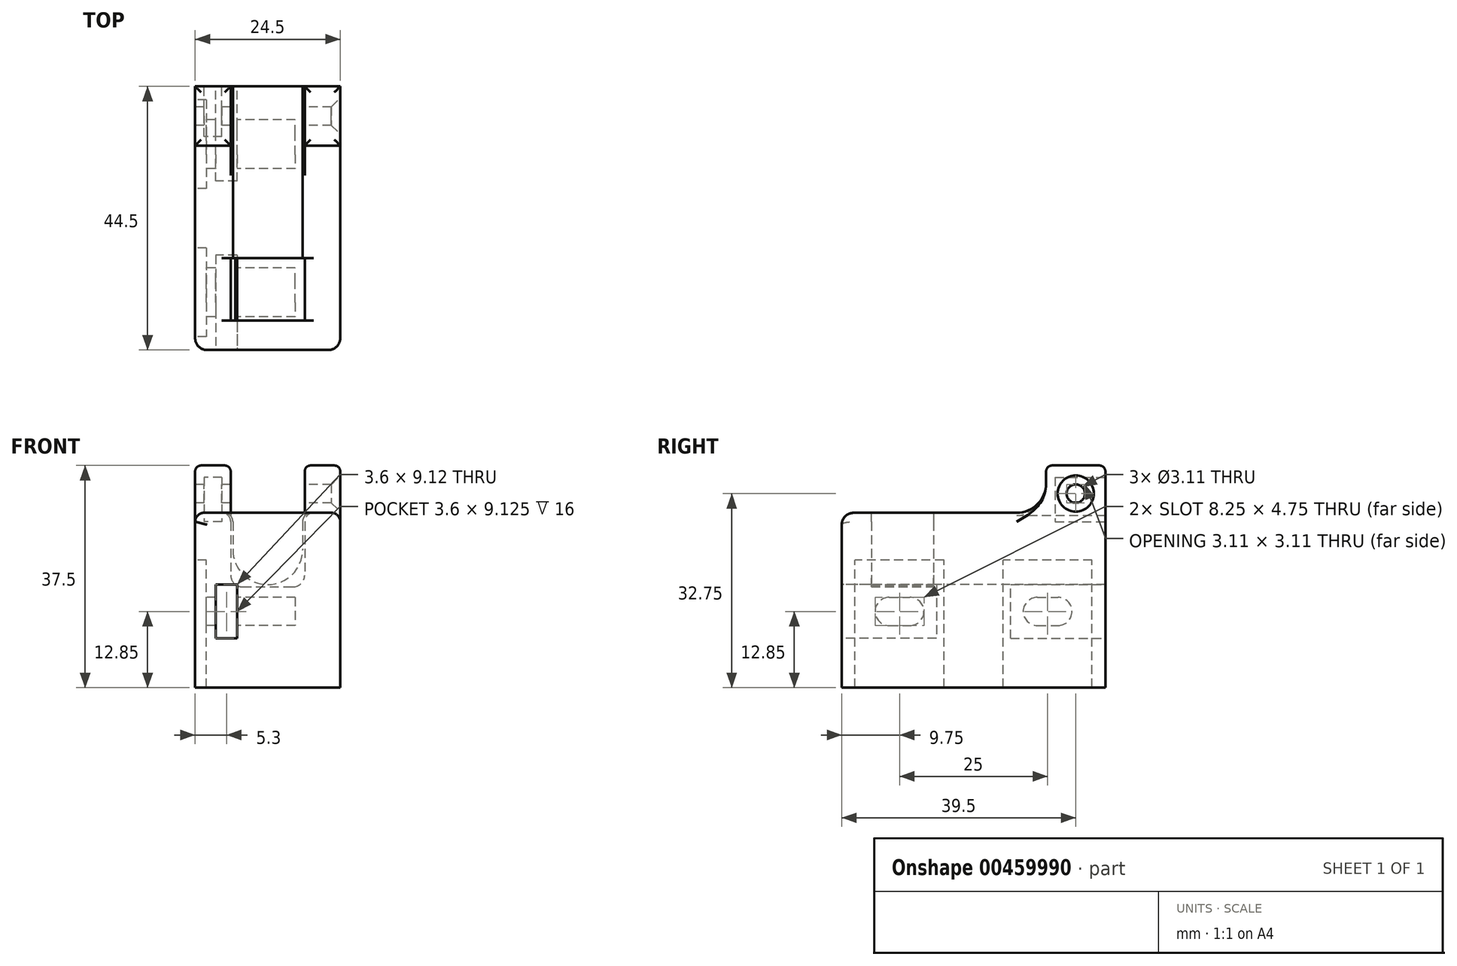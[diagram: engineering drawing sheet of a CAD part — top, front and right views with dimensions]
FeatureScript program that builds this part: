
annotation { "Feature Type Name" : "Feature", "Feature Type Description" : "" }
export const myFeature = defineFeature(function(context is Context, id is Id, definition is map)
    precondition{}
    {
        {
            var Q0;
            Q0=qCreatedBy(makeId("Front.planeOp"),FACE);
            var sketch = newSketch(context, id + "F0", { "sketchPlane" : qUnion([Q0])});
            skLineSegment(sketch, "E0.bottom", {"start": v(-6.25, 6.25) * mm, "end": v(6.25, 6.25) * mm, "construction": true});
            skLineSegment(sketch, "E0.top", {"start": v(-4.25, -6.25) * mm, "end": v(4.25, -6.25) * mm});
            skLineSegment(sketch, "E0.left", {"start": v(-6.25, 4.75) * mm, "end": v(-6.25, -4.25) * mm});
            skLineSegment(sketch, "E0.right", {"start": v(6.25, 4.75) * mm, "end": v(6.25, -4.25) * mm});
            skPoint(sketch, "E0.middle", {"position": v(0, 0) * mm});
            skLineSegment(sketch, "E1.bottom", {"start": v(-10.75, -11.25) * mm, "end": v(10.75, -11.25) * mm});
            skLineSegment(sketch, "E1.left", {"start": v(-12.25, -9.75) * mm, "end": v(-12.25, 4.75) * mm});
            skLineSegment(sketch, "E1.right", {"start": v(12.25, -9.75) * mm, "end": v(12.25, 4.75) * mm});
            skLineSegment(sketch, "E2", {"start": v(-7.75, 6.25) * mm, "end": v(-10.75, 6.25) * mm});
            skLineSegment(sketch, "E3", {"start": v(7.75, 6.25) * mm, "end": v(10.75, 6.25) * mm});
            skPoint(sketch, "E4.visualSharp", {"position": v(-6.25, -6.25) * mm});
            skArc(sketch, "E4.filletArc", {"start": v(-6.25, -4.25) * mm, "mid": v(-5.66, -5.66) * mm, "end": v(-4.25, -6.25) * mm});
            skPoint(sketch, "E5.visualSharp", {"position": v(6.25, -6.25) * mm});
            skArc(sketch, "E5.filletArc", {"start": v(4.25, -6.25) * mm, "mid": v(5.66, -5.66) * mm, "end": v(6.25, -4.25) * mm});
            skPoint(sketch, "E6.visualSharp", {"position": v(-6.25, 6.25) * mm});
            skArc(sketch, "E6.filletArc", {"start": v(-6.25, 4.75) * mm, "mid": v(-6.69, 5.81) * mm, "end": v(-7.75, 6.25) * mm});
            skPoint(sketch, "E7.visualSharp", {"position": v(6.25, 6.25) * mm});
            skArc(sketch, "E7.filletArc", {"start": v(7.75, 6.25) * mm, "mid": v(6.69, 5.81) * mm, "end": v(6.25, 4.75) * mm});
            skLineSegment(sketch, "E8", {"start": v(6.25, 0.25) * mm, "end": v(12.25, 0.25) * mm, "construction": true});
            skLineSegment(sketch, "E9", {"start": v(-6.25, 0.25) * mm, "end": v(-12.25, 0.25) * mm, "construction": true});
            skLineSegment(sketch, "E10", {"start": v(0, -6.25) * mm, "end": v(0, -11.25) * mm, "construction": true});
            skPoint(sketch, "E11.visualSharp", {"position": v(-12.25, 6.25) * mm});
            skArc(sketch, "E11.filletArc", {"start": v(-10.75, 6.25) * mm, "mid": v(-11.81, 5.81) * mm, "end": v(-12.25, 4.75) * mm});
            skPoint(sketch, "E12.visualSharp", {"position": v(-12.25, -11.25) * mm});
            skArc(sketch, "E12.filletArc", {"start": v(-12.25, -9.75) * mm, "mid": v(-11.81, -10.81) * mm, "end": v(-10.75, -11.25) * mm});
            skPoint(sketch, "E13.visualSharp", {"position": v(12.25, -11.25) * mm});
            skArc(sketch, "E13.filletArc", {"start": v(10.75, -11.25) * mm, "mid": v(11.81, -10.81) * mm, "end": v(12.25, -9.75) * mm});
            skPoint(sketch, "E14.visualSharp", {"position": v(12.25, 6.25) * mm});
            skArc(sketch, "E14.filletArc", {"start": v(12.25, 4.75) * mm, "mid": v(11.81, 5.81) * mm, "end": v(10.75, 6.25) * mm});
            skSolve(sketch);
        }
        {
            var Q0;
            Q0=makeQuery(id+"F0.imprint","IMPRINT",FACE,{"disambiguationData":[TD([[makeQuery(id+"F0.imprint","IMPRINT",EDGE,{"derivedFrom":sQuery(id+"F0.wireOp",EDGE,"E0.top")}),-1.0]])]});
            extrude(context, id + "F1", {"entities" : qUnion([Q0]), "depth" : 10.5 * mm});
        }
        {
            var Q0;
            Q0=makeQuery(id+"F1.opExtrude","CAP_FACE",FACE,{"disambiguationData":[OSD([sQuery(id+"F0.wireOp",EDGE,"E0.top"),sQuery(id+"F0.wireOp",EDGE,"E0.left"),sQuery(id+"F0.wireOp",EDGE,"E0.right"),sQuery(id+"F0.wireOp",EDGE,"E1.bottom"),sQuery(id+"F0.wireOp",EDGE,"E1.left"),sQuery(id+"F0.wireOp",EDGE,"E1.right"),sQuery(id+"F0.wireOp",EDGE,"E2"),sQuery(id+"F0.wireOp",EDGE,"E3"),sQuery(id+"F0.wireOp",EDGE,"E4.filletArc"),sQuery(id+"F0.wireOp",EDGE,"E5.filletArc"),sQuery(id+"F0.wireOp",EDGE,"E6.filletArc"),sQuery(id+"F0.wireOp",EDGE,"E7.filletArc"),sQuery(id+"F0.wireOp",EDGE,"E11.filletArc"),sQuery(id+"F0.wireOp",EDGE,"E12.filletArc"),sQuery(id+"F0.wireOp",EDGE,"E13.filletArc"),sQuery(id+"F0.wireOp",EDGE,"E14.filletArc")])],"isStart":false});
            var sketch = newSketch(context, id + "F2", { "sketchPlane" : qUnion([Q0])});
            skLineSegment(sketch, "E15.bottom", {"start": v(-10.75, -11.25) * mm, "end": v(10.75, -11.25) * mm});
            skLineSegment(sketch, "E15.top", {"start": v(-10.75, 6.25) * mm, "end": v(10.75, 6.25) * mm});
            skLineSegment(sketch, "E15.left", {"start": v(-12.25, -9.75) * mm, "end": v(-12.25, 4.75) * mm});
            skLineSegment(sketch, "E15.right", {"start": v(12.25, -9.75) * mm, "end": v(12.25, 4.75) * mm});
            skPoint(sketch, "E16.visualSharp", {"position": v(-12.25, 6.25) * mm});
            skArc(sketch, "E16.filletArc", {"start": v(-10.75, 6.25) * mm, "mid": v(-11.81, 5.81) * mm, "end": v(-12.25, 4.75) * mm});
            skPoint(sketch, "E17.visualSharp", {"position": v(-12.25, -11.25) * mm});
            skArc(sketch, "E17.filletArc", {"start": v(-12.25, -9.75) * mm, "mid": v(-11.81, -10.81) * mm, "end": v(-10.75, -11.25) * mm});
            skPoint(sketch, "E18.visualSharp", {"position": v(12.25, -11.25) * mm});
            skArc(sketch, "E18.filletArc", {"start": v(10.75, -11.25) * mm, "mid": v(11.81, -10.81) * mm, "end": v(12.25, -9.75) * mm});
            skPoint(sketch, "E19.visualSharp", {"position": v(12.25, 6.25) * mm});
            skArc(sketch, "E19.filletArc", {"start": v(12.25, 4.75) * mm, "mid": v(11.81, 5.81) * mm, "end": v(10.75, 6.25) * mm});
            skSolve(sketch);
        }
        {
            var Q0;
            Q0 = qSketchRegion(id + "F2", true);
            extrude(context, id + "F3", {"entities" : qUnion([Q0]), "operationType" : NewBodyOperationType.ADD, "depth" : 5 * mm, "offsetDistance" : 25 * mm});
        }
        {
            var Q0;
            Q0=makeQuery(id+"F3.opExtrude","SWEPT_FACE",FACE,{"disambiguationData":[OSD([sQuery(id+"F2.wireOp",EDGE,"E15.top")])]});
            var sketch = newSketch(context, id + "F4", { "sketchPlane" : qUnion([Q0])});
            skLineSegment(sketch, "E20", {"start": v(-87.92, 24.65) * mm, "end": v(-21.67, -10.5) * mm});
            skLineSegment(sketch, "E21", {"start": v(-21.67, -10.5) * mm, "end": v(-33.58, -32.94) * mm});
            skLineSegment(sketch, "E22", {"start": v(-33.58, -32.94) * mm, "end": v(-99.83, 2.22) * mm});
            skLineSegment(sketch, "E23", {"start": v(-99.83, 2.22) * mm, "end": v(-87.92, 24.65) * mm});
            skLineSegment(sketch, "E24", {"start": v(-21.67, -10.5) * mm, "end": v(-87.92, -10.5) * mm, "construction": true});
            skLineSegment(sketch, "E25", {"start": v(-87.92, 24.65) * mm, "end": v(-87.92, -10.5) * mm, "construction": true});
            skLineSegment(sketch, "E26", {"start": v(-12.25, -10.5) * mm, "end": v(-12.25, -15.5) * mm, "construction": true});
            skLineSegment(sketch, "E27", {"start": v(12.25, -10.5) * mm, "end": v(12.25, -28.5) * mm, "construction": true});
            skSolve(sketch);
        }
        {
            var Q0;
            Q0 = qSketchRegion(id + "F4", true);
            extrude(context, id + "F5", {"entities" : qUnion([Q0]), "operationType" : NewBodyOperationType.REMOVE, "oppositeDirection" : true, "depth" : 25 * mm});
        }
        {
            var Q0;
            Q0=makeQuery(id+"F1.opExtrude","CAP_FACE",FACE,{"disambiguationData":[OSD([sQuery(id+"F0.wireOp",EDGE,"E0.top"),sQuery(id+"F0.wireOp",EDGE,"E0.left"),sQuery(id+"F0.wireOp",EDGE,"E0.right"),sQuery(id+"F0.wireOp",EDGE,"E1.bottom"),sQuery(id+"F0.wireOp",EDGE,"E1.left"),sQuery(id+"F0.wireOp",EDGE,"E1.right"),sQuery(id+"F0.wireOp",EDGE,"E2"),sQuery(id+"F0.wireOp",EDGE,"E3"),sQuery(id+"F0.wireOp",EDGE,"E4.filletArc"),sQuery(id+"F0.wireOp",EDGE,"E5.filletArc"),sQuery(id+"F0.wireOp",EDGE,"E6.filletArc"),sQuery(id+"F0.wireOp",EDGE,"E7.filletArc"),sQuery(id+"F0.wireOp",EDGE,"E11.filletArc"),sQuery(id+"F0.wireOp",EDGE,"E12.filletArc"),sQuery(id+"F0.wireOp",EDGE,"E13.filletArc"),sQuery(id+"F0.wireOp",EDGE,"E14.filletArc")])],"isStart":true});
            var sketch = newSketch(context, id + "F6", { "sketchPlane" : qUnion([Q0])});
            skArc(sketch, "E28", {"start": v(-5.88, 0) * mm, "mid": v(0, -5.88) * mm, "end": v(5.88, 0) * mm});
            skPoint(sketch, "E29", {"position": v(6.69, 5.81) * mm});
            skLineSegment(sketch, "E30.top", {"start": v(-10.75, -11.25) * mm, "end": v(10.75, -11.25) * mm});
            skLineSegment(sketch, "E30.left", {"start": v(-12.25, 4.75) * mm, "end": v(-12.25, -9.75) * mm});
            skLineSegment(sketch, "E30.right", {"start": v(12.25, 4.75) * mm, "end": v(12.25, -9.75) * mm});
            skLineSegment(sketch, "E31", {"start": v(-10.75, 6.25) * mm, "end": v(-7.38, 6.25) * mm});
            skLineSegment(sketch, "E32", {"start": v(-5.87, 4.75) * mm, "end": v(-5.87, 0) * mm});
            skLineSegment(sketch, "E33", {"start": v(10.75, 6.25) * mm, "end": v(7.38, 6.25) * mm});
            skLineSegment(sketch, "E34", {"start": v(5.87, 4.75) * mm, "end": v(5.88, 0) * mm});
            skPoint(sketch, "E35.visualSharp", {"position": v(-12.25, 6.25) * mm});
            skArc(sketch, "E35.filletArc", {"start": v(-10.75, 6.25) * mm, "mid": v(-11.81, 5.81) * mm, "end": v(-12.25, 4.75) * mm});
            skPoint(sketch, "E36.visualSharp", {"position": v(-5.88, 6.25) * mm});
            skArc(sketch, "E36.filletArc", {"start": v(-5.88, 4.75) * mm, "mid": v(-6.31, 5.81) * mm, "end": v(-7.38, 6.25) * mm});
            skPoint(sketch, "E37.visualSharp", {"position": v(5.88, 6.25) * mm});
            skArc(sketch, "E37.filletArc", {"start": v(7.38, 6.25) * mm, "mid": v(6.31, 5.81) * mm, "end": v(5.88, 4.75) * mm});
            skPoint(sketch, "E38.visualSharp", {"position": v(12.25, 6.25) * mm});
            skArc(sketch, "E38.filletArc", {"start": v(12.25, 4.75) * mm, "mid": v(11.81, 5.81) * mm, "end": v(10.75, 6.25) * mm});
            skPoint(sketch, "E39.visualSharp", {"position": v(12.25, -11.25) * mm});
            skArc(sketch, "E39.filletArc", {"start": v(10.75, -11.25) * mm, "mid": v(11.81, -10.81) * mm, "end": v(12.25, -9.75) * mm});
            skPoint(sketch, "E40.visualSharp", {"position": v(-12.25, -11.25) * mm});
            skArc(sketch, "E40.filletArc", {"start": v(-12.25, -9.75) * mm, "mid": v(-11.81, -10.81) * mm, "end": v(-10.75, -11.25) * mm});
            skSolve(sketch);
        }
        {
            var Q0;
            Q0 = qSketchRegion(id + "F6", true);
            extrude(context, id + "F7", {"entities" : qUnion([Q0]), "operationType" : NewBodyOperationType.ADD, "depth" : 29 * mm, "offsetDistance" : 25 * mm});
        }
        {
            var Q0;
            Q0=makeQuery(id+"F3.opExtrude","CAP_FACE",FACE,{"disambiguationData":[OSD([sQuery(id+"F2.wireOp",EDGE,"E15.bottom"),sQuery(id+"F2.wireOp",EDGE,"E15.top"),sQuery(id+"F2.wireOp",EDGE,"E15.left"),sQuery(id+"F2.wireOp",EDGE,"E15.right"),sQuery(id+"F2.wireOp",EDGE,"E16.filletArc"),sQuery(id+"F2.wireOp",EDGE,"E17.filletArc"),sQuery(id+"F2.wireOp",EDGE,"E18.filletArc"),sQuery(id+"F2.wireOp",EDGE,"E19.filletArc")])],"isStart":false});
            fillet(context, id + "F8", {"entities" : qUnion([Q0]), "radius" : 2 * mm, "tangentPropagation" : true, "allowEdgeOverflow" : false});
        }
        {
            var Q0;
            Q0=makeQuery(id+"F7.boolean.opBoolean","MERGE",FACE,{"derivedFrom":[makeQuery(id+"F3.boolean.opBoolean","MERGE",FACE,{"derivedFrom":[makeQuery(id+"F1.opExtrude","SWEPT_FACE",FACE,{"disambiguationData":[OSD([sQuery(id+"F0.wireOp",EDGE,"E2")])]}),makeQuery(id+"F1.opExtrude","SWEPT_FACE",FACE,{"disambiguationData":[OSD([sQuery(id+"F0.wireOp",EDGE,"E3")])]}),makeQuery(id+"F3.opExtrude","SWEPT_FACE",FACE,{"disambiguationData":[OSD([sQuery(id+"F2.wireOp",EDGE,"E15.top")])]})]}),makeQuery(id+"F7.opExtrude","SWEPT_FACE",FACE,{"disambiguationData":[OSD([sQuery(id+"F6.wireOp",EDGE,"E31")])]}),makeQuery(id+"F7.opExtrude","SWEPT_FACE",FACE,{"disambiguationData":[OSD([sQuery(id+"F6.wireOp",EDGE,"E33")])]})]});
            var sketch = newSketch(context, id + "F9", { "sketchPlane" : qUnion([Q0])});
            skLineSegment(sketch, "E41.bottom", {"start": v(-12.25, 29) * mm, "end": v(-6.25, 29) * mm});
            skLineSegment(sketch, "E41.top", {"start": v(-12.25, 19) * mm, "end": v(-6.25, 19) * mm});
            skLineSegment(sketch, "E41.left", {"start": v(-12.25, 29) * mm, "end": v(-12.25, 19) * mm});
            skLineSegment(sketch, "E41.right", {"start": v(-6.25, 29) * mm, "end": v(-6.25, 19) * mm});
            skLineSegment(sketch, "E42.bottom", {"start": v(6.25, 29) * mm, "end": v(12.25, 29) * mm});
            skLineSegment(sketch, "E42.top", {"start": v(6.25, 19) * mm, "end": v(12.25, 19) * mm});
            skLineSegment(sketch, "E42.left", {"start": v(6.25, 29) * mm, "end": v(6.25, 19) * mm});
            skLineSegment(sketch, "E42.right", {"start": v(12.25, 29) * mm, "end": v(12.25, 19) * mm});
            skSolve(sketch);
        }
        {
            var Q0;
            Q0 = qSketchRegion(id + "F9", true);
            extrude(context, id + "F10", {"entities" : qUnion([Q0]), "operationType" : NewBodyOperationType.ADD, "depth" : 8 * mm, "hasSecondDirection" : true, "secondDirectionBound" : SecondDirectionBoundingType.UP_TO_NEXT, "secondDirectionOppositeDirection" : true, "secondDirectionDepth" : 25 * mm, "offsetDistance" : 25 * mm});
        }
        {
            var Q0;
            Q0=makeQuery(id+"F10.boolean.opBoolean","MERGE",FACE,{"derivedFrom":[makeQuery(id+"F7.opExtrude","CAP_FACE",FACE,{"disambiguationData":[OSD([sQuery(id+"F6.wireOp",EDGE,"E28"),sQuery(id+"F6.wireOp",EDGE,"E30.top"),sQuery(id+"F6.wireOp",EDGE,"E30.left"),sQuery(id+"F6.wireOp",EDGE,"E30.right"),sQuery(id+"F6.wireOp",EDGE,"E31"),sQuery(id+"F6.wireOp",EDGE,"E32"),sQuery(id+"F6.wireOp",EDGE,"E33"),sQuery(id+"F6.wireOp",EDGE,"E34"),sQuery(id+"F6.wireOp",EDGE,"E35.filletArc"),sQuery(id+"F6.wireOp",EDGE,"E36.filletArc"),sQuery(id+"F6.wireOp",EDGE,"E37.filletArc"),sQuery(id+"F6.wireOp",EDGE,"E38.filletArc"),sQuery(id+"F6.wireOp",EDGE,"E39.filletArc"),sQuery(id+"F6.wireOp",EDGE,"E40.filletArc")])],"isStart":false}),makeQuery(id+"F10.opExtrude","SWEPT_FACE",FACE,{"disambiguationData":[OSD([sQuery(id+"F9.wireOp",EDGE,"E41.bottom")])]}),makeQuery(id+"F10.opExtrude","SWEPT_FACE",FACE,{"disambiguationData":[OSD([sQuery(id+"F9.wireOp",EDGE,"E42.bottom")])]})]});
            var sketch = newSketch(context, id + "F11", { "sketchPlane" : qUnion([Q0])});
            skLineSegment(sketch, "E43.bottom", {"start": v(7.75, 12.25) * mm, "end": v(10.75, 12.25) * mm});
            skLineSegment(sketch, "E43.top", {"start": v(7.75, 4.75) * mm, "end": v(10.75, 4.75) * mm});
            skLineSegment(sketch, "E43.left", {"start": v(7.75, 12.25) * mm, "end": v(7.75, 4.75) * mm});
            skLineSegment(sketch, "E43.right", {"start": v(10.75, 12.25) * mm, "end": v(10.75, 4.75) * mm});
            skPoint(sketch, "E44", {"position": v(9.25, 12.25) * mm});
            skPoint(sketch, "E45", {"position": v(9.25, 14.25) * mm});
            skPoint(sketch, "E46.endSnap0", {"position": v(9.25, 4.75) * mm});
            skPoint(sketch, "E47", {"position": v(10.75, 8.5) * mm});
            skCircle(sketch, "E48", {"center": v(0, 0) * mm, "radius": 5.88 * mm, "construction": true});
            skLineSegment(sketch, "E49", {"start": v(12.25, 8.5) * mm, "end": v(-12.25, 8.5) * mm, "construction": true});
            skSolve(sketch);
        }
        {
            var Q0;
            Q0 = qSketchRegion(id + "F11", true);
            extrude(context, id + "F12", {"entities" : qUnion([Q0]), "operationType" : NewBodyOperationType.REMOVE, "oppositeDirection" : true, "depth" : 5 * mm + (6.35 * 1.1 * 0.5) * mm});
        }
        {
            var Q0;
            Q0=makeQuery(id+"F10.boolean.opBoolean","MERGE",FACE,{"derivedFrom":[makeQuery(id+"F7.boolean.opBoolean","MERGE",FACE,{"derivedFrom":[makeQuery(id+"F3.boolean.opBoolean","MERGE",FACE,{"derivedFrom":[makeQuery(id+"F1.opExtrude","SWEPT_FACE",FACE,{"disambiguationData":[OSD([sQuery(id+"F0.wireOp",EDGE,"E1.left")])]}),makeQuery(id+"F3.opExtrude","SWEPT_FACE",FACE,{"disambiguationData":[OSD([sQuery(id+"F2.wireOp",EDGE,"E15.left")])]})]}),makeQuery(id+"F7.opExtrude","SWEPT_FACE",FACE,{"disambiguationData":[OSD([sQuery(id+"F6.wireOp",EDGE,"E30.right")])]})]}),makeQuery(id+"F10.opExtrude","SWEPT_FACE",FACE,{"disambiguationData":[OSD([sQuery(id+"F9.wireOp",EDGE,"E41.left")])]})]});
            var sketch = newSketch(context, id + "F13", { "sketchPlane" : qUnion([Q0])});
            skLineSegment(sketch, "E50", {"start": v(-24, 14.25) * mm, "end": v(-24, 4.75) * mm, "construction": true});
            skPoint(sketch, "E51", {"position": v(-24, 9.5) * mm});
            skCircle(sketch, "E52", {"center": v(-24, 9.5) * mm, "radius": 1.55 * mm});
            skLineSegment(sketch, "E53", {"start": v(-29, 4.75) * mm, "end": v(-19, 4.75) * mm, "construction": true});
            skLineSegment(sketch, "E54", {"start": v(-19, 4.75) * mm, "end": v(-19, 4.75) * mm});
            skSolve(sketch);
        }
        {
            var Q0;
            Q0 = qSketchRegion(id + "F13", true);
            extrude(context, id + "F14", {"entities" : qUnion([Q0]), "operationType" : NewBodyOperationType.REMOVE, "endBound" : BoundingType.THROUGH_ALL, "oppositeDirection" : true, "depth" : 25 * mm});
        }
        {
            var Q0;
            Q0=makeQuery(id+"F10.boolean.opBoolean","MERGE",FACE,{"derivedFrom":[makeQuery(id+"F7.boolean.opBoolean","MERGE",FACE,{"derivedFrom":[makeQuery(id+"F3.boolean.opBoolean","MERGE",FACE,{"derivedFrom":[makeQuery(id+"F1.opExtrude","SWEPT_FACE",FACE,{"disambiguationData":[OSD([sQuery(id+"F0.wireOp",EDGE,"E1.right")])]}),makeQuery(id+"F3.opExtrude","SWEPT_FACE",FACE,{"disambiguationData":[OSD([sQuery(id+"F2.wireOp",EDGE,"E15.right")])]})]}),makeQuery(id+"F7.opExtrude","SWEPT_FACE",FACE,{"disambiguationData":[OSD([sQuery(id+"F6.wireOp",EDGE,"E30.left")])]})]}),makeQuery(id+"F10.opExtrude","SWEPT_FACE",FACE,{"disambiguationData":[OSD([sQuery(id+"F9.wireOp",EDGE,"E42.right")])]})]});
            var sketch = newSketch(context, id + "F15", { "sketchPlane" : qUnion([Q0])});
            skCircle(sketch, "E55", {"center": v(24, 9.5) * mm, "radius": 2.53 * mm});
            skSolve(sketch);
        }
        {
            var Q0;
            Q0=makeQuery(id+"F10.boolean.opBoolean","MERGE",FACE,{"derivedFrom":[makeQuery(id+"F7.opExtrude","CAP_FACE",FACE,{"disambiguationData":[OSD([sQuery(id+"F6.wireOp",EDGE,"E28"),sQuery(id+"F6.wireOp",EDGE,"E30.top"),sQuery(id+"F6.wireOp",EDGE,"E30.left"),sQuery(id+"F6.wireOp",EDGE,"E30.right"),sQuery(id+"F6.wireOp",EDGE,"E31"),sQuery(id+"F6.wireOp",EDGE,"E32"),sQuery(id+"F6.wireOp",EDGE,"E33"),sQuery(id+"F6.wireOp",EDGE,"E34"),sQuery(id+"F6.wireOp",EDGE,"E35.filletArc"),sQuery(id+"F6.wireOp",EDGE,"E36.filletArc"),sQuery(id+"F6.wireOp",EDGE,"E37.filletArc"),sQuery(id+"F6.wireOp",EDGE,"E38.filletArc"),sQuery(id+"F6.wireOp",EDGE,"E39.filletArc"),sQuery(id+"F6.wireOp",EDGE,"E40.filletArc")])],"isStart":false}),makeQuery(id+"F10.opExtrude","SWEPT_FACE",FACE,{"disambiguationData":[OSD([sQuery(id+"F9.wireOp",EDGE,"E41.bottom")])]}),makeQuery(id+"F10.opExtrude","SWEPT_FACE",FACE,{"disambiguationData":[OSD([sQuery(id+"F9.wireOp",EDGE,"E42.bottom")])]})]});
            var sketch = newSketch(context, id + "F16", { "sketchPlane" : qUnion([Q0])});
            skLineSegment(sketch, "E56", {"start": v(10.75, 8.5) * mm, "end": v(-12.25, 8.5) * mm, "construction": true});
            skPoint(sketch, "E57", {"position": v(7.75, 8.5) * mm});
            skSolve(sketch);
        }
        {
            var Q0;
            Q0=makeQuery(id+"F14.boolean.opBoolean","INTERSECT",EDGE,{"derivedFrom":[makeQuery(id+"F10.boolean.opBoolean","MERGE",FACE,{"derivedFrom":[makeQuery(id+"F7.boolean.opBoolean","MERGE",FACE,{"derivedFrom":[makeQuery(id+"F3.boolean.opBoolean","MERGE",FACE,{"derivedFrom":[makeQuery(id+"F1.opExtrude","SWEPT_FACE",FACE,{"disambiguationData":[OSD([sQuery(id+"F0.wireOp",EDGE,"E1.right")])]}),makeQuery(id+"F3.opExtrude","SWEPT_FACE",FACE,{"disambiguationData":[OSD([sQuery(id+"F2.wireOp",EDGE,"E15.right")])]})]}),makeQuery(id+"F7.opExtrude","SWEPT_FACE",FACE,{"disambiguationData":[OSD([sQuery(id+"F6.wireOp",EDGE,"E30.left")])]})]}),makeQuery(id+"F10.opExtrude","SWEPT_FACE",FACE,{"disambiguationData":[OSD([sQuery(id+"F9.wireOp",EDGE,"E42.right")])]})]}),makeQuery(id+"F14.opExtrude","SWEPT_FACE",FACE,{"disambiguationData":[OSD([sQuery(id+"F13.wireOp",EDGE,"E52")])]})]});
            chamfer(context, id + "F17", {"entities" : qUnion([Q0]), "width" : 1.5 * mm, "tangentPropagation" : true});
        }
        {
            var Q0;
            Q0=makeQuery(id+"F10.opExtrude","CAP_FACE",FACE,{"disambiguationData":[OSD([sQuery(id+"F9.wireOp",EDGE,"E42.bottom"),sQuery(id+"F9.wireOp",EDGE,"E42.top"),sQuery(id+"F9.wireOp",EDGE,"E42.left"),sQuery(id+"F9.wireOp",EDGE,"E42.right")])],"isStart":false});
            var Q1;
            Q1=makeQuery(id+"F10.opExtrude","CAP_FACE",FACE,{"disambiguationData":[OSD([sQuery(id+"F9.wireOp",EDGE,"E41.bottom"),sQuery(id+"F9.wireOp",EDGE,"E41.top"),sQuery(id+"F9.wireOp",EDGE,"E41.left"),sQuery(id+"F9.wireOp",EDGE,"E41.right")])],"isStart":false});
            fillet(context, id + "F18", {"entities" : qUnion([Q0, Q1]), "radius" : 1 * mm, "tangentPropagation" : true, "allowEdgeOverflow" : false});
        }
        {
            var Q0;
            Q0=makeQuery(id+"F7.boolean.opBoolean","MERGE",FACE,{"derivedFrom":[makeQuery(id+"F3.boolean.opBoolean","MERGE",FACE,{"derivedFrom":[makeQuery(id+"F1.opExtrude","SWEPT_FACE",FACE,{"disambiguationData":[OSD([sQuery(id+"F0.wireOp",EDGE,"E1.bottom")])]}),makeQuery(id+"F3.opExtrude","SWEPT_FACE",FACE,{"disambiguationData":[OSD([sQuery(id+"F2.wireOp",EDGE,"E15.bottom")])]})]}),makeQuery(id+"F7.opExtrude","SWEPT_FACE",FACE,{"disambiguationData":[OSD([sQuery(id+"F6.wireOp",EDGE,"E30.top")])]})]});
            var sketch = newSketch(context, id + "F19", { "sketchPlane" : qUnion([Q0])});
            skLineSegment(sketch, "E58.bottom", {"start": v(12.25, -29) * mm, "end": v(-12.25, -29) * mm});
            skLineSegment(sketch, "E58.top", {"start": v(12.25, 15.5) * mm, "end": v(-12.25, 15.5) * mm});
            skLineSegment(sketch, "E58.left", {"start": v(12.25, -29) * mm, "end": v(12.25, 15.5) * mm});
            skLineSegment(sketch, "E58.right", {"start": v(-12.25, -29) * mm, "end": v(-12.25, 15.5) * mm});
            skSolve(sketch);
        }
        {
            var Q0;
            Q0 = qSketchRegion(id + "F19", true);
            var Q1;
            Q1=makeQuery(id+"F7.boolean.opBoolean","MERGE",FACE,{"derivedFrom":[makeQuery(id+"F3.boolean.opBoolean","MERGE",FACE,{"derivedFrom":[makeQuery(id+"F1.opExtrude","SWEPT_FACE",FACE,{"disambiguationData":[OSD([sQuery(id+"F0.wireOp",EDGE,"E13.filletArc")])]}),makeQuery(id+"F3.opExtrude","SWEPT_FACE",FACE,{"disambiguationData":[OSD([sQuery(id+"F2.wireOp",EDGE,"E18.filletArc")])]})]}),makeQuery(id+"F7.opExtrude","SWEPT_FACE",FACE,{"disambiguationData":[OSD([sQuery(id+"F6.wireOp",EDGE,"E40.filletArc")])]})]});
            var Q2;
            Q2=makeQuery(id+"F1.opExtrude","SWEPT_BODY",BODY,{"disambiguationData":[OSD([sQuery(id+"F0.wireOp",EDGE,"E0.top"),sQuery(id+"F0.wireOp",EDGE,"E0.left"),sQuery(id+"F0.wireOp",EDGE,"E0.right"),sQuery(id+"F0.wireOp",EDGE,"E1.bottom"),sQuery(id+"F0.wireOp",EDGE,"E1.left"),sQuery(id+"F0.wireOp",EDGE,"E1.right"),sQuery(id+"F0.wireOp",EDGE,"E2"),sQuery(id+"F0.wireOp",EDGE,"E3"),sQuery(id+"F0.wireOp",EDGE,"E4.filletArc"),sQuery(id+"F0.wireOp",EDGE,"E5.filletArc"),sQuery(id+"F0.wireOp",EDGE,"E6.filletArc"),sQuery(id+"F0.wireOp",EDGE,"E7.filletArc"),sQuery(id+"F0.wireOp",EDGE,"E11.filletArc"),sQuery(id+"F0.wireOp",EDGE,"E12.filletArc"),sQuery(id+"F0.wireOp",EDGE,"E13.filletArc"),sQuery(id+"F0.wireOp",EDGE,"E14.filletArc")])]});
            extrude(context, id + "F20", {"entities" : qUnion([Q0]), "operationType" : NewBodyOperationType.ADD, "depth" : 12 * mm, "offsetDistance" : 25 * mm, "hasSecondDirection" : true, "secondDirectionOppositeDirection" : true, "secondDirectionDepth" : 2 * mm, "secondDirectionBoundEntityFace" : qUnion([Q1]), "secondDirectionBoundEntityBody" : qUnion([Q2])});
        }
        {
            var Q0;
            Q0=makeQuery(id+"F20.opExtrude","SWEPT_EDGE",EDGE,{"disambiguationData":[OSD([sQuery(id+"F19.wireOp",EDGE,"E58.top"),sQuery(id+"F19.wireOp",EDGE,"E58.left")])]});
            var Q1;
            Q1=makeQuery(id+"F20.opExtrude","SWEPT_EDGE",EDGE,{"disambiguationData":[OSD([sQuery(id+"F19.wireOp",EDGE,"E58.top"),sQuery(id+"F19.wireOp",EDGE,"E58.right")])]});
            fillet(context, id + "F21", {"entities" : qUnion([Q0, Q1]), "radius" : 2 * mm, "allowEdgeOverflow" : false});
        }
        {
            var Q0;
            Q0=makeQuery(id+"F20.boolean.opBoolean","MERGE",FACE,{"derivedFrom":[makeQuery(id+"F10.boolean.opBoolean","MERGE",FACE,{"derivedFrom":[makeQuery(id+"F7.boolean.opBoolean","MERGE",FACE,{"derivedFrom":[makeQuery(id+"F3.boolean.opBoolean","MERGE",FACE,{"derivedFrom":[makeQuery(id+"F1.opExtrude","SWEPT_FACE",FACE,{"disambiguationData":[OSD([sQuery(id+"F0.wireOp",EDGE,"E1.left")])]}),makeQuery(id+"F3.opExtrude","SWEPT_FACE",FACE,{"disambiguationData":[OSD([sQuery(id+"F2.wireOp",EDGE,"E15.left")])]})]}),makeQuery(id+"F7.opExtrude","SWEPT_FACE",FACE,{"disambiguationData":[OSD([sQuery(id+"F6.wireOp",EDGE,"E30.right")])]})]}),makeQuery(id+"F10.opExtrude","SWEPT_FACE",FACE,{"disambiguationData":[OSD([sQuery(id+"F9.wireOp",EDGE,"E41.left")])]})]}),makeQuery(id+"F20.opExtrude","SWEPT_FACE",FACE,{"disambiguationData":[OSD([sQuery(id+"F19.wireOp",EDGE,"E58.right")])]})]});
            var sketch = newSketch(context, id + "F22", { "sketchPlane" : qUnion([Q0])});
            skLineSegment(sketch, "E59.bottom", {"start": v(-26.75, -23.25) * mm, "end": v(-11.75, -23.25) * mm});
            skLineSegment(sketch, "E59.top", {"start": v(-26.75, -1.75) * mm, "end": v(-11.75, -1.75) * mm});
            skLineSegment(sketch, "E59.left", {"start": v(-26.75, -23.25) * mm, "end": v(-26.75, -1.75) * mm});
            skLineSegment(sketch, "E59.right", {"start": v(-11.75, -23.25) * mm, "end": v(-11.75, -1.75) * mm});
            skLineSegment(sketch, "E60.bottom", {"start": v(-1.75, -23.25) * mm, "end": v(13.25, -23.25) * mm});
            skLineSegment(sketch, "E60.top", {"start": v(-1.75, -1.75) * mm, "end": v(13.25, -1.75) * mm});
            skLineSegment(sketch, "E60.left", {"start": v(-1.75, -23.25) * mm, "end": v(-1.75, -1.75) * mm});
            skLineSegment(sketch, "E60.right", {"start": v(13.25, -23.25) * mm, "end": v(13.25, -1.75) * mm});
            skPoint(sketch, "E61", {"position": v(-19.25, -1.75) * mm});
            skPoint(sketch, "E62", {"position": v(5.75, -1.75) * mm});
            skLineSegment(sketch, "E63", {"start": v(-19.25, -12.5) * mm, "end": v(5.75, -12.5) * mm, "construction": true});
            skPoint(sketch, "E63.startSnap0", {"position": v(-11.75, -12.5) * mm});
            skLineSegment(sketch, "E64", {"start": v(-29, 2.52) * mm, "end": v(15.5, 2.52) * mm, "construction": true});
            skPoint(sketch, "E65", {"position": v(-6.75, 2.52) * mm});
            skPoint(sketch, "E66", {"position": v(-6.75, -12.5) * mm});
            skSolve(sketch);
        }
        {
            var Q0;
            Q0 = qSketchRegion(id + "F22", true);
            extrude(context, id + "F23", {"entities" : qUnion([Q0]), "operationType" : NewBodyOperationType.REMOVE, "oppositeDirection" : true, "depth" : 1.9 * mm, "offsetDistance" : 25 * mm});
        }
        {
            var Q0;
            Q0=makeQuery(id+"F23.boolean.opBoolean","COPY",FACE,{"derivedFrom":makeQuery(id+"F23.opExtrude","CAP_FACE",FACE,{"disambiguationData":[OSD([sQuery(id+"F22.wireOp",EDGE,"E59.bottom"),sQuery(id+"F22.wireOp",EDGE,"E59.top"),sQuery(id+"F22.wireOp",EDGE,"E59.left"),sQuery(id+"F22.wireOp",EDGE,"E59.right")])],"isStart":false})});
            var sketch = newSketch(context, id + "F24", { "sketchPlane" : qUnion([Q0])});
            skLineSegment(sketch, "E67", {"start": v(-19.25, -1.75) * mm, "end": v(-19.25, -23.25) * mm, "construction": true});
            skLineSegment(sketch, "E68", {"start": v(5.75, -1.75) * mm, "end": v(5.75, -23.25) * mm, "construction": true});
            skCircle(sketch, "E69", {"center": v(-19.25, -10.4) * mm, "radius": 2.38 * mm, "construction": true});
            skCircle(sketch, "E70", {"center": v(5.75, -10.4) * mm, "radius": 2.38 * mm, "construction": true});
            skLineSegment(sketch, "E71", {"start": v(-19.25, -8.03) * mm, "end": v(-21, -8.03) * mm});
            skLineSegment(sketch, "E72", {"start": v(-21, -8.03) * mm, "end": v(-17.5, -8.03) * mm});
            skLineSegment(sketch, "E73", {"start": v(-19.25, -12.78) * mm, "end": v(-21, -12.78) * mm});
            skLineSegment(sketch, "E74", {"start": v(-21, -12.78) * mm, "end": v(-17.5, -12.78) * mm});
            skArc(sketch, "E75", {"start": v(-21, -8.03) * mm, "mid": v(-23.37, -10.4) * mm, "end": v(-21, -12.78) * mm});
            skArc(sketch, "E76", {"start": v(-17.5, -12.77) * mm, "mid": v(-15.12, -10.4) * mm, "end": v(-17.5, -8.03) * mm});
            skLineSegment(sketch, "E77", {"start": v(-19.25, -10.4) * mm, "end": v(-21, -10.4) * mm, "construction": true});
            skLineSegment(sketch, "E78", {"start": v(-17.5, -10.4) * mm, "end": v(-19.25, -10.4) * mm, "construction": true});
            skLineSegment(sketch, "E79", {"start": v(5.75, -8.02) * mm, "end": v(4, -8.02) * mm});
            skLineSegment(sketch, "E80", {"start": v(4, -8.02) * mm, "end": v(7.5, -8.02) * mm});
            skLineSegment(sketch, "E81", {"start": v(5.75, -12.77) * mm, "end": v(4, -12.77) * mm});
            skLineSegment(sketch, "E82", {"start": v(4, -12.77) * mm, "end": v(7.5, -12.77) * mm});
            skArc(sketch, "E83", {"start": v(4, -8.03) * mm, "mid": v(1.62, -10.4) * mm, "end": v(4, -12.78) * mm});
            skArc(sketch, "E84", {"start": v(7.5, -12.77) * mm, "mid": v(9.87, -10.4) * mm, "end": v(7.5, -8.03) * mm});
            skLineSegment(sketch, "E85", {"start": v(5.75, -10.4) * mm, "end": v(4, -10.4) * mm, "construction": true});
            skLineSegment(sketch, "E86", {"start": v(7.5, -10.4) * mm, "end": v(5.75, -10.4) * mm, "construction": true});
            skSolve(sketch);
        }
        {
            var Q0;
            Q0=makeQuery(id+"F16.imprint","IMPRINT",FACE,{"disambiguationData":[TD([[makeQuery(id+"F16.imprint","IMPRINT",EDGE,{"derivedFrom":makeQuery(id+"F7.opExtrude","CAP_EDGE",EDGE,{"disambiguationData":[OSD([sQuery(id+"F6.wireOp",EDGE,"E28")])],"isStart":false})}),-1.0]])]});
            var sketch = newSketch(context, id + "F25", { "sketchPlane" : qUnion([Q0])});
            skLineSegment(sketch, "E87.bottom", {"start": v(5.15, -14.96) * mm, "end": v(8.75, -14.96) * mm});
            skLineSegment(sketch, "E87.top", {"start": v(5.15, -5.84) * mm, "end": v(8.75, -5.84) * mm});
            skLineSegment(sketch, "E87.left", {"start": v(5.15, -14.96) * mm, "end": v(5.15, -5.84) * mm});
            skLineSegment(sketch, "E87.right", {"start": v(8.75, -14.96) * mm, "end": v(8.75, -5.84) * mm});
            skPoint(sketch, "E88", {"position": v(8.75, -10.4) * mm});
            skSolve(sketch);
        }
        {
            var Q0;
            Q0=makeQuery(id+"F20.boolean.opBoolean","MERGE",FACE,{"derivedFrom":[makeQuery(id+"F3.opExtrude","CAP_FACE",FACE,{"disambiguationData":[OSD([sQuery(id+"F2.wireOp",EDGE,"E15.bottom"),sQuery(id+"F2.wireOp",EDGE,"E15.top"),sQuery(id+"F2.wireOp",EDGE,"E15.left"),sQuery(id+"F2.wireOp",EDGE,"E15.right"),sQuery(id+"F2.wireOp",EDGE,"E16.filletArc"),sQuery(id+"F2.wireOp",EDGE,"E17.filletArc"),sQuery(id+"F2.wireOp",EDGE,"E18.filletArc"),sQuery(id+"F2.wireOp",EDGE,"E19.filletArc")])],"isStart":false}),makeQuery(id+"F20.opExtrude","SWEPT_FACE",FACE,{"disambiguationData":[OSD([sQuery(id+"F19.wireOp",EDGE,"E58.top")])]})]});
            var sketch = newSketch(context, id + "F26", { "sketchPlane" : qUnion([Q0])});
            skLineSegment(sketch, "E89.bottom", {"start": v(-5.15, -5.84) * mm, "end": v(-8.75, -5.84) * mm});
            skLineSegment(sketch, "E89.top", {"start": v(-5.15, -14.96) * mm, "end": v(-8.75, -14.96) * mm});
            skLineSegment(sketch, "E89.left", {"start": v(-5.15, -5.84) * mm, "end": v(-5.15, -14.96) * mm});
            skLineSegment(sketch, "E89.right", {"start": v(-8.75, -5.84) * mm, "end": v(-8.75, -14.96) * mm});
            skSolve(sketch);
        }
        {
            var Q0;
            Q0 = qSketchRegion(id + "F25", true);
            extrude(context, id + "F27", {"entities" : qUnion([Q0]), "operationType" : NewBodyOperationType.REMOVE, "oppositeDirection" : true, "depth" : 16 * mm, "offsetDistance" : 25 * mm});
        }
        {
            var Q0;
            Q0 = qSketchRegion(id + "F26", true);
            extrude(context, id + "F28", {"entities" : qUnion([Q0]), "operationType" : NewBodyOperationType.REMOVE, "oppositeDirection" : true, "depth" : 16 * mm, "offsetDistance" : 25 * mm});
        }
        {
            var Q0;
            Q0 = qSketchRegion(id + "F24", true);
            var Q1;
            Q1=sQuery(id+"F24.wireOp",EDGE,"E69");
            extrude(context, id + "F29", {"entities" : qUnion([Q0]), "operationType" : NewBodyOperationType.REMOVE, "surfaceEntities" : qUnion([Q1]), "oppositeDirection" : true, "depth" : 15 * mm, "offsetDistance" : 25 * mm});
        }
        {
            var Q0;
            Q0=makeQuery(id+"F10.boolean.opBoolean","INTERSECT",EDGE,{"derivedFrom":[makeQuery(id+"F7.boolean.opBoolean","MERGE",FACE,{"derivedFrom":[makeQuery(id+"F3.boolean.opBoolean","MERGE",FACE,{"derivedFrom":[makeQuery(id+"F1.opExtrude","SWEPT_FACE",FACE,{"disambiguationData":[OSD([sQuery(id+"F0.wireOp",EDGE,"E2")])]}),makeQuery(id+"F1.opExtrude","SWEPT_FACE",FACE,{"disambiguationData":[OSD([sQuery(id+"F0.wireOp",EDGE,"E3")])]}),makeQuery(id+"F3.opExtrude","SWEPT_FACE",FACE,{"disambiguationData":[OSD([sQuery(id+"F2.wireOp",EDGE,"E15.top")])]})]}),makeQuery(id+"F7.opExtrude","SWEPT_FACE",FACE,{"disambiguationData":[OSD([sQuery(id+"F6.wireOp",EDGE,"E31")])]}),makeQuery(id+"F7.opExtrude","SWEPT_FACE",FACE,{"disambiguationData":[OSD([sQuery(id+"F6.wireOp",EDGE,"E33")])]})]}),makeQuery(id+"F10.opExtrude","SWEPT_FACE",FACE,{"disambiguationData":[OSD([sQuery(id+"F9.wireOp",EDGE,"E41.top")])]})]});
            var Q1;
            Q1=makeQuery(id+"F10.boolean.opBoolean","INTERSECT",EDGE,{"derivedFrom":[makeQuery(id+"F7.boolean.opBoolean","MERGE",FACE,{"derivedFrom":[makeQuery(id+"F3.boolean.opBoolean","MERGE",FACE,{"derivedFrom":[makeQuery(id+"F1.opExtrude","SWEPT_FACE",FACE,{"disambiguationData":[OSD([sQuery(id+"F0.wireOp",EDGE,"E2")])]}),makeQuery(id+"F1.opExtrude","SWEPT_FACE",FACE,{"disambiguationData":[OSD([sQuery(id+"F0.wireOp",EDGE,"E3")])]}),makeQuery(id+"F3.opExtrude","SWEPT_FACE",FACE,{"disambiguationData":[OSD([sQuery(id+"F2.wireOp",EDGE,"E15.top")])]})]}),makeQuery(id+"F7.opExtrude","SWEPT_FACE",FACE,{"disambiguationData":[OSD([sQuery(id+"F6.wireOp",EDGE,"E31")])]}),makeQuery(id+"F7.opExtrude","SWEPT_FACE",FACE,{"disambiguationData":[OSD([sQuery(id+"F6.wireOp",EDGE,"E33")])]})]}),makeQuery(id+"F10.opExtrude","SWEPT_FACE",FACE,{"disambiguationData":[OSD([sQuery(id+"F9.wireOp",EDGE,"E42.top")])]})]});
            fillet(context, id + "F30", {"entities" : qUnion([Q0, Q1]), "radius" : 5 * mm, "tangentPropagation" : true, "allowEdgeOverflow" : false});
        }
    });
